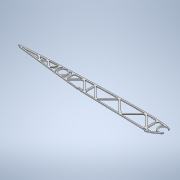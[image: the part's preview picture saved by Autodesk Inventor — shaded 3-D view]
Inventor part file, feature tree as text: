
AUTODESK INVENTOR PART (.ipt)
format: ipt  version: 2022 (Build 260153000, 153)  size: 466,432 bytes
history: native  units: mm
features: extrude x1, sketch x1
ambient origin geometry x8: Origin, YZ Plane, XZ Plane, XY Plane, X Axis, Y Axis, Z Axis, Center Point
bodies: Body1 (feature_tree)
feature tree (2):
  extrude  "Extrusion5"  Depth=10.0mm
  sketch  "Sketch1"  dims[d31=34.456mm d50=368.759386mm d57=16.0mm d69=8.0mm d80=19.0mm d81=16.0mm d82=1.0mm d83=1.0mm d84=1.0mm d85=1.0mm d86=1.0mm d87=0.8mm d88=1.0mm d90=19.0mm d94=5.0mm d95=5.0mm d105=5.0mm d106=5.0mm d108=2.0mm d114=5.0mm d115=5.0mm d116=24.0mm d117=2.5mm d118=2.5mm d123=2.5mm d124=2.5mm d125=10.0mm d126=24.0mm d127=24.0mm d128=27.0mm d135=0.5mm d139=7.0mm d169=27.0mm d181=45.0deg d185=7.0mm d186=45.0deg d190=7.0mm d191=45.0deg d206=90.0deg d212=90.0deg d215=7.0mm d216=90.0deg d219=7.0mm d220=2.0mm d221=0.0mm]
